# Revit family: xxxUrinal-Blowout-American_Standard-Lynbrook-6601012.020
name_source: partatom
category: Plumbing Fixtures
units: mm (PartAtom-declared; Revit-internal decimal feet)

## family parameters
Cut with Voids When Loaded = No
Host = Face
OmniClass Number = 23.45.05.21.11.21
OmniClass Title = Urinals
Part Type = Normal
Room Calculation Point = No
Round Connector Dimension = Use Diameter
Shared = Yes

## types (1)
- 6601012.020
    ADA Compliant = Yes
    ASME A112.19.2M for Vitreous China Fixtures = Yes
    Assembly Code = D2010210
    CW Connection = Yes
    CWFU = 5
    Cold Water Connection Diameter = 1"
    Cold Water Connection Height = 11 1/2"
    Cold Water Connection Width = 4 3/4"
    Default Elevation = 0"
    Description = Lynbrook™ 1.0 gpf/3.8 Lpf Top Spud Blowout Urinal
    Finish = Vitreous China-American Standard-020-White
    Flush Rate = 1.0 gpf (3.8 Lpf), Low Water Usage
    Flush Requirement = 0.7 to 1.0 GPF
    HW Connection = No
    HWFU = 0
    Height = 28 3/4"
    Installation Type = Wall Hung
    Length = 14"
    Manufacturer = American Standard
    Material = Vitreous China-American Standard-020-White
    Model = 6601012.020
    Mounting Height (Max. 24") = 24"
    Mounting Height Constraint = 17"
    Price = Prices may vary. Please consult Manufacturer Representative for most up-to-date price list.
    Product Documentation Link = https://americanstandard.box.com
    Product Page URL = https://www.americanstandard-us.com
    Recommended Working Pressure = 20 psi at valve when flushing and 80 psi static
    Revised Date = 01/04/2022
    URL = https://www.americanstandard-us.com
    Vent Connection = No
    WFU = 5
    Waste Connection = Yes
    Waste Connection Diameter = 2"
    Width = 18 1/2"

## geometry (parser evidence)
native form markers: Sweep x2
no freeform markers — native parametric forms only
